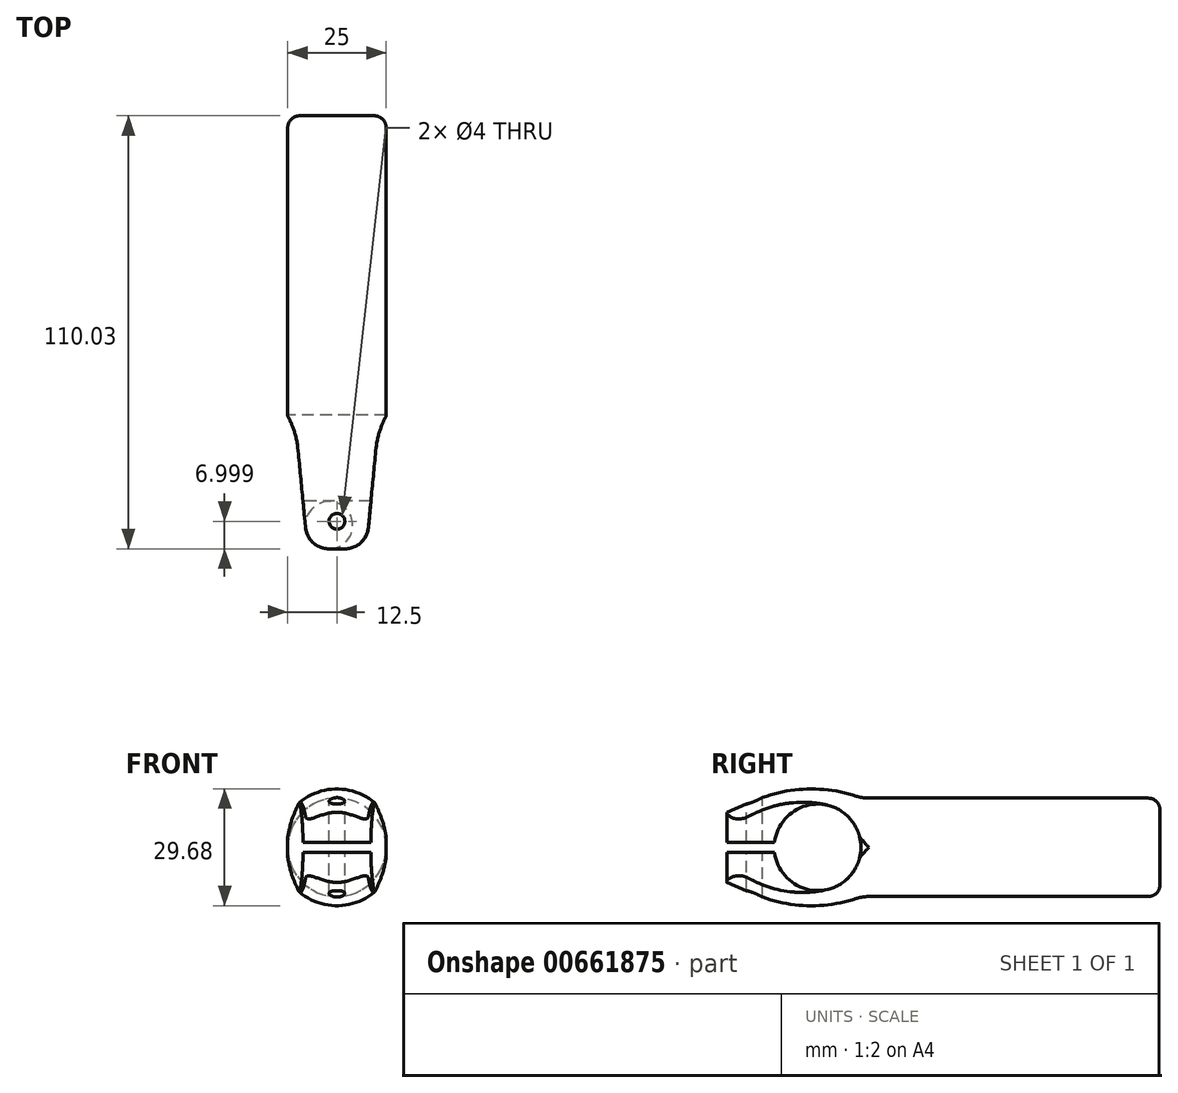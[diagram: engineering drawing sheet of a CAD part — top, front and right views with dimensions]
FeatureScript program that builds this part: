
annotation { "Feature Type Name" : "Feature", "Feature Type Description" : "" }
export const myFeature = defineFeature(function(context is Context, id is Id, definition is map)
    precondition{}
    {
        {
            var Q0;
            Q0=qCreatedBy(makeId("Right.planeOp"),FACE);
            var sketch = newSketch(context, id + "F0", { "sketchPlane" : qUnion([Q0])});
            skArc(sketch, "E0", {"start": v(11, 0) * mm, "mid": v(0.66, 10.98) * mm, "end": v(-10.92, 1.31) * mm});
            skLineSegment(sketch, "E1", {"start": v(-23.03, 8.93) * mm, "end": v(-15.53, 12.04) * mm});
            skLineSegment(sketch, "E2", {"start": v(-23.03, 8.93) * mm, "end": v(-23.03, 1.31) * mm});
            skLineSegment(sketch, "E3", {"start": v(-23.03, 1.31) * mm, "end": v(-10.92, 1.31) * mm});
            skArc(sketch, "E4", {"start": v(13, 12.5) * mm, "mid": v(-1.31, 15) * mm, "end": v(-15.53, 12.04) * mm});
            skLineSegment(sketch, "E5", {"start": v(13, 12.5) * mm, "end": v(13, 0) * mm});
            skLineSegment(sketch, "E6", {"start": v(13, 0) * mm, "end": v(11, 0) * mm});
            skLineSegment(sketch, "E7", {"start": v(0, 0) * mm, "end": v(11, 0) * mm, "construction": true});
            skLineSegment(sketch, "E8", {"start": v(0, 15) * mm, "end": v(0, 0) * mm, "construction": true});
            skSolve(sketch);
        }
        {
            var Q0;
            Q0 = qSketchRegion(id + "F0", true);
            extrude(context, id + "F1", {"entities" : qUnion([Q0]), "depth" : 25 * mm, "offsetDistance" : 25 * mm, "symmetric" : true});
        }
        {
            var Q0;
            Q0=makeQuery(id+"F1.opExtrude","SWEPT_BODY",BODY,{"disambiguationData":[OSD([sQuery(id+"F0.wireOp",EDGE,"E0"),sQuery(id+"F0.wireOp",EDGE,"E1"),sQuery(id+"F0.wireOp",EDGE,"E2"),sQuery(id+"F0.wireOp",EDGE,"E3"),sQuery(id+"F0.wireOp",EDGE,"E4"),sQuery(id+"F0.wireOp",EDGE,"E5"),sQuery(id+"F0.wireOp",EDGE,"E6")])]});
            var Q1;
            Q1=qCreatedBy(makeId("Top.planeOp"),FACE);
            mirror(context, id + "F2", {"operationType" : NewBodyOperationType.ADD, "entities" : qUnion([Q0]), "mirrorPlane" : qUnion([Q1])});
        }
        {
            var Q0;
            {var subQ0=makeQuery(id+"F1.opExtrude","SWEPT_FACE",FACE,{"disambiguationData":[OSD([sQuery(id+"F0.wireOp",EDGE,"E5")])]});Q0=makeQuery(id+"F2.boolean.opBoolean","MERGE",FACE,{"derivedFrom":[subQ0,makeQuery(id+"F2.opPattern","COPY",FACE,{"derivedFrom":subQ0,"instanceName":"1"})]});}
            var sketch = newSketch(context, id + "F3", { "sketchPlane" : qUnion([Q0])});
            skCircle(sketch, "E9", {"center": v(0, 0) * mm, "radius": 12.5 * mm});
            skSolve(sketch);
        }
        {
            var Q0;
            Q0 = qSketchRegion(id + "F3", true);
            extrude(context, id + "F4", {"entities" : qUnion([Q0]), "operationType" : NewBodyOperationType.ADD, "depth" : 74 * mm, "offsetDistance" : 25 * mm});
        }
        {
            var Q0;
            Q0=makeQuery(id+"F1.opExtrude","CAP_EDGE",EDGE,{"disambiguationData":[OSD([sQuery(id+"F0.wireOp",EDGE,"E2")])],"isStart":false});
            var Q1;
            Q1=makeQuery(id+"F1.opExtrude","CAP_EDGE",EDGE,{"disambiguationData":[OSD([sQuery(id+"F0.wireOp",EDGE,"E2")])],"isStart":true});
            var Q2;
            Q2=makeQuery(id+"F2.opPattern","COPY",EDGE,{"derivedFrom":makeQuery(id+"F1.opExtrude","CAP_EDGE",EDGE,{"disambiguationData":[OSD([sQuery(id+"F0.wireOp",EDGE,"E2")])],"isStart":true}),"instanceName":"1"});
            var Q3;
            Q3=makeQuery(id+"F2.opPattern","COPY",EDGE,{"derivedFrom":makeQuery(id+"F1.opExtrude","CAP_EDGE",EDGE,{"disambiguationData":[OSD([sQuery(id+"F0.wireOp",EDGE,"E2")])],"isStart":false}),"instanceName":"1"});
            fillet(context, id + "F5", {"entities" : qUnion([Q0, Q1, Q2, Q3]), "radius" : 10 * mm, "tangentPropagation" : true, "allowEdgeOverflow" : false});
        }
        {
            var Q0;
            Q0=qCreatedBy(makeId("Right.planeOp"),FACE);
            var sketch = newSketch(context, id + "F6", { "sketchPlane" : qUnion([Q0])});
            skLineSegment(sketch, "E10", {"start": v(13, 12.5) * mm, "end": v(46, 12.5) * mm});
            skLineSegment(sketch, "E11", {"start": v(-23.03, 22.5) * mm, "end": v(46, 22.5) * mm});
            skLineSegment(sketch, "E12", {"start": v(46, 22.5) * mm, "end": v(46, 12.5) * mm});
            skLineSegment(sketch, "E13", {"start": v(0, 0) * mm, "end": v(26.85, 0) * mm, "construction": true});
            skArc(sketch, "E14", {"start": v(9.87, 13) * mm, "mid": v(11.41, 12.63) * mm, "end": v(13, 12.5) * mm});
            skArc(sketch, "E15", {"start": v(9.87, 13) * mm, "mid": v(-2.92, 14.81) * mm, "end": v(-15.53, 12.04) * mm});
            skLineSegment(sketch, "E16", {"start": v(-15.53, 12.04) * mm, "end": v(-23.03, 8.93) * mm});
            skLineSegment(sketch, "E17", {"start": v(-23.03, 8.93) * mm, "end": v(-23.03, 22.5) * mm});
            skSolve(sketch);
        }
        {
            var Q0;
            Q0=makeQuery(id+"F6.imprint","IMPRINT",FACE,{"disambiguationData":[TD([[makeQuery(id+"F6.imprint","IMPRINT",EDGE,{"derivedFrom":sQuery(id+"F6.wireOp",EDGE,"E10")}),1.0]])]});
            var Q1;
            Q1=sQuery(id+"F6.wireOp",EDGE,"E13");
            var Q2;
            Q2=sQuery(id+"F0.wireOp",EDGE,"E7");
            revolve(context, id + "F7", {"operationType" : NewBodyOperationType.REMOVE, "surfaceOperationType" : NewSurfaceOperationType.NEW, "entities" : qUnion([Q0]), "surfaceEntities" : qUnion([Q1]), "axis" : qUnion([Q2]), "revolveType" : RevolveType.FULL, "oppositeDirection" : true});
        }
        {
            var Q0;
            Q0=qCreatedBy(makeId("Top.planeOp"),FACE);
            var sketch = newSketch(context, id + "F8", { "sketchPlane" : qUnion([Q0])});
            skCircle(sketch, "E18", {"center": v(0, -16.03) * mm, "radius": 2 * mm});
            skLineSegment(sketch, "E19", {"start": v(-9.95, 2.67) * mm, "end": v(-7.97, -17.61) * mm});
            skLineSegment(sketch, "E20", {"start": v(-2, -23.03) * mm, "end": v(2, -23.03) * mm});
            skLineSegment(sketch, "E21", {"start": v(7.97, -17.61) * mm, "end": v(9.95, 2.67) * mm});
            skLineSegment(sketch, "E22", {"start": v(9.95, 2.67) * mm, "end": v(25, 0) * mm});
            skLineSegment(sketch, "E23", {"start": v(25, 0) * mm, "end": v(25, -50) * mm});
            skLineSegment(sketch, "E24", {"start": v(25, -50) * mm, "end": v(-25, -50) * mm});
            skLineSegment(sketch, "E25", {"start": v(-25, -50) * mm, "end": v(-25, 0) * mm});
            skLineSegment(sketch, "E26", {"start": v(-25, 0) * mm, "end": v(-9.95, 2.67) * mm});
            skLineSegment(sketch, "E27", {"start": v(0, -16.03) * mm, "end": v(0, -50) * mm, "construction": true});
            skPoint(sketch, "E28.visualSharp", {"position": v(-7.44, -23.03) * mm});
            skArc(sketch, "E28.filletArc", {"start": v(-7.97, -17.61) * mm, "mid": v(-6.03, -21.47) * mm, "end": v(-2, -23.03) * mm});
            skPoint(sketch, "E29.visualSharp", {"position": v(7.44, -23.03) * mm});
            skArc(sketch, "E29.filletArc", {"start": v(2, -23.03) * mm, "mid": v(6.03, -21.47) * mm, "end": v(7.97, -17.61) * mm});
            skSolve(sketch);
        }
        {
            var Q0;
            Q0 = qSketchRegion(id + "F8", true);
            extrude(context, id + "F9", {"entities" : qUnion([Q0]), "operationType" : NewBodyOperationType.REMOVE, "oppositeDirection" : true, "depth" : 50 * mm, "offsetDistance" : 25 * mm, "symmetric" : true});
        }
        {
            var Q0;
            Q0=makeQuery(id+"F4.opExtrude","CAP_EDGE",EDGE,{"disambiguationData":[OSD([sQuery(id+"F3.wireOp",EDGE,"E9")])],"isStart":false});
            fillet(context, id + "F10", {"entities" : qUnion([Q0]), "radius" : 3 * mm, "tangentPropagation" : true, "allowEdgeOverflow" : false});
        }
    });
